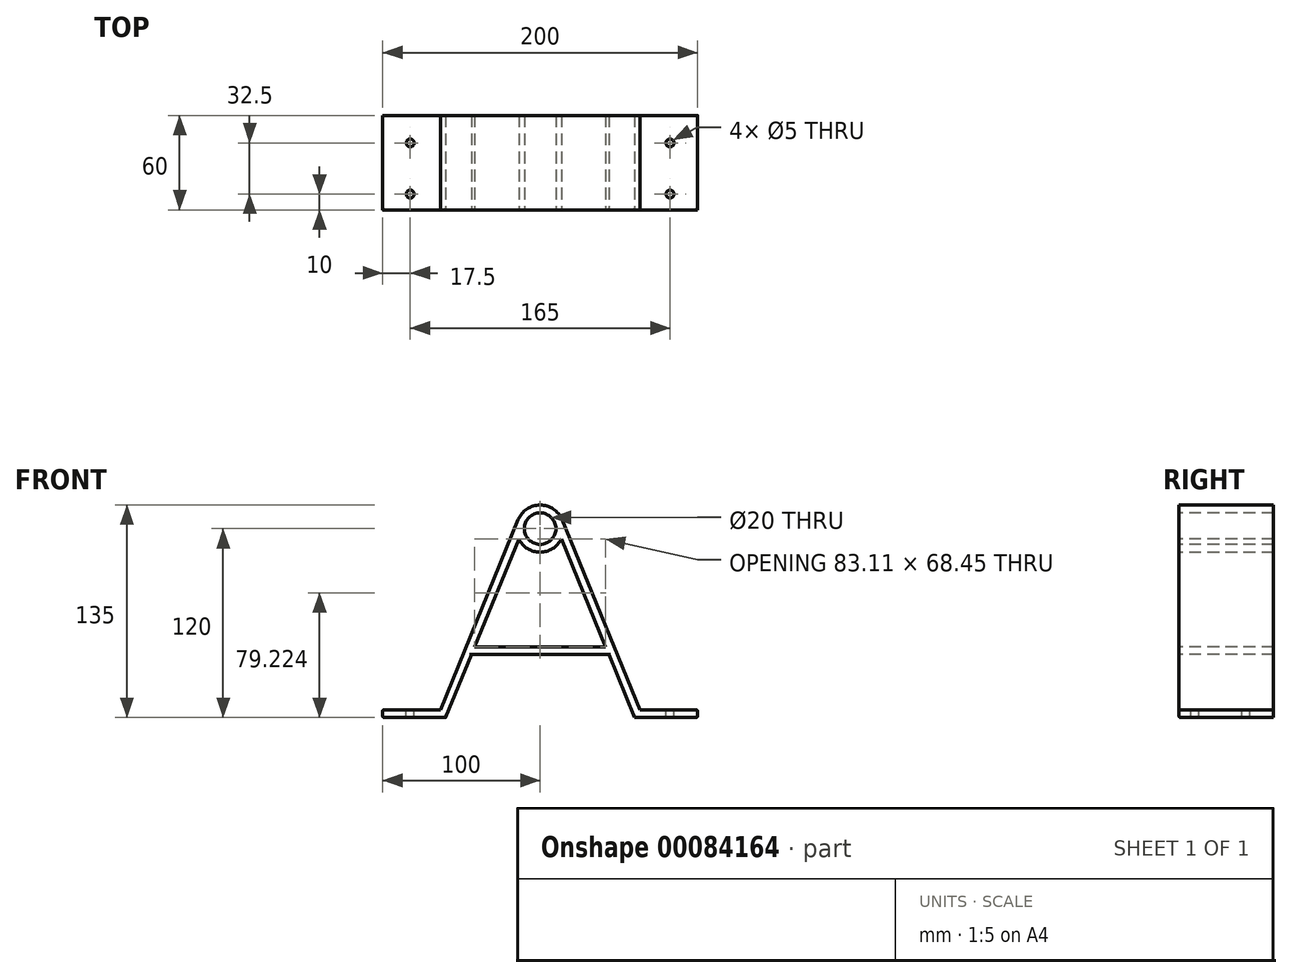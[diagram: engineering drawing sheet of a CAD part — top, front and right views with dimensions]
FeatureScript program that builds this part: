
annotation { "Feature Type Name" : "Feature", "Feature Type Description" : "" }
export const myFeature = defineFeature(function(context is Context, id is Id, definition is map)
    precondition{}
    {
        {
            var Q0;
            Q0=qCreatedBy(makeId("Front.planeOp"),FACE);
            var sketch = newSketch(context, id + "F0", { "sketchPlane" : qUnion([Q0])});
            skArc(sketch, "E0", {"start": v(86.5, 108.45) * mm, "mid": v(100, 100) * mm, "end": v(113.5, 108.45) * mm});
            skLineSegment(sketch, "E1", {"start": v(0, 0) * mm, "end": v(36.65, 0) * mm});
            skLineSegment(sketch, "E2", {"start": v(36.65, 0) * mm, "end": v(86.12, 120.69) * mm});
            skLineSegment(sketch, "E3", {"start": v(0, 0) * mm, "end": v(0, -5) * mm});
            skLineSegment(sketch, "E4", {"start": v(0, -5) * mm, "end": v(40, -5) * mm});
            skLineSegment(sketch, "E5", {"start": v(40, -5) * mm, "end": v(56.4, 35) * mm});
            skLineSegment(sketch, "E6", {"start": v(100, 115) * mm, "end": v(100, -58.47) * mm, "construction": true});
            skLineSegment(sketch, "E7.MirrorCS", {"start": v(160, -5) * mm, "end": v(143.6, 35) * mm});
            skLineSegment(sketch, "E8.MirrorCS", {"start": v(163.35, 0) * mm, "end": v(113.88, 120.69) * mm});
            skLineSegment(sketch, "E9.MirrorCS", {"start": v(200, 0) * mm, "end": v(163.35, 0) * mm});
            skLineSegment(sketch, "E10.MirrorCS", {"start": v(200, -5) * mm, "end": v(160, -5) * mm});
            skLineSegment(sketch, "E11.MirrorCS", {"start": v(200, 0) * mm, "end": v(200, -5) * mm});
            skCircle(sketch, "E12", {"center": v(100, 115) * mm, "radius": 10 * mm});
            skLineSegment(sketch, "E13", {"start": v(58.45, 40) * mm, "end": v(141.55, 40) * mm});
            skLineSegment(sketch, "E14", {"start": v(56.4, 35) * mm, "end": v(143.6, 35) * mm});
            skLineSegment(sketch, "E15.trimOffspring", {"start": v(58.45, 40) * mm, "end": v(86.5, 108.45) * mm});
            skLineSegment(sketch, "E16.trimOffspring", {"start": v(141.55, 40) * mm, "end": v(113.5, 108.45) * mm});
            skArc(sketch, "E17.trimOffspring", {"start": v(113.88, 120.69) * mm, "mid": v(100, 130) * mm, "end": v(86.12, 120.69) * mm});
            skLineSegment(sketch, "E18", {"start": v(160, -5) * mm, "end": v(200, -5) * mm});
            skLineSegment(sketch, "E19", {"start": v(199.82, 0.68) * mm, "end": v(163.35, 0) * mm});
            skArc(sketch, "E20", {"start": v(100, 130) * mm, "mid": v(91.64, 102.54) * mm, "end": v(113.88, 120.69) * mm});
            skLineSegment(sketch, "E21", {"start": v(86.12, 120.69) * mm, "end": v(36.65, 0) * mm});
            skSolve(sketch);
        }
        {
            var Q0;
            Q0=qSketchRegion(id+"F0",true);
            extrude(context, id + "F1", {"entities" : qUnion([Q0]), "oppositeDirection" : true, "depth" : 60 * mm});
        }
        {
            var Q0;
            Q0=makeQuery(id+"F1.opExtrude","SWEPT_FACE",FACE,{"disambiguationData":[OSD([sQuery(id+"F0.wireOp",EDGE,"E9.MirrorCS")])]});
            var sketch = newSketch(context, id + "F2", { "sketchPlane" : qUnion([Q0])});
            skCircle(sketch, "E22", {"center": v(182.5, 10) * mm, "radius": 2.5 * mm});
            skCircle(sketch, "E23", {"center": v(182.5, 42.5) * mm, "radius": 2.5 * mm});
            skLineSegment(sketch, "E24", {"start": v(100, 0) * mm, "end": v(100, 124.34) * mm, "construction": true});
            skCircle(sketch, "E25.MirrorC", {"center": v(17.5, 10) * mm, "radius": 2.5 * mm});
            skCircle(sketch, "E26.MirrorC", {"center": v(17.5, 42.5) * mm, "radius": 2.5 * mm});
            skSolve(sketch);
        }
        {
            var Q0;
            Q0=qSketchRegion(id+"F2",true);
            extrude(context, id + "F3", {"entities" : qUnion([Q0]), "operationType" : NewBodyOperationType.REMOVE, "endBound" : BoundingType.THROUGH_ALL, "oppositeDirection" : true, "depth" : 25 * mm});
        }
        {
            var Q0;
            Q0=makeQuery(id+"F1.opExtrude","SWEPT_EDGE",EDGE,{"disambiguationData":[OSD([sQuery(id+"F0.wireOp",EDGE,"E9.MirrorCS"),sQuery(id+"F0.wireOp",EDGE,"E11.MirrorCS")])]});
            var Q1;
            Q1=makeQuery(id+"F1.opExtrude","SWEPT_EDGE",EDGE,{"disambiguationData":[OSD([sQuery(id+"F0.wireOp",EDGE,"E10.MirrorCS"),sQuery(id+"F0.wireOp",EDGE,"E11.MirrorCS")])]});
            var Q2;
            Q2=makeQuery(id+"F1.opExtrude","SWEPT_EDGE",EDGE,{"disambiguationData":[OSD([sQuery(id+"F0.wireOp",EDGE,"E1"),sQuery(id+"F0.wireOp",EDGE,"E3")])]});
            var Q3;
            Q3=makeQuery(id+"F1.opExtrude","SWEPT_EDGE",EDGE,{"disambiguationData":[OSD([sQuery(id+"F0.wireOp",EDGE,"E3"),sQuery(id+"F0.wireOp",EDGE,"E4")])]});
            var Q4;
            Q4=makeQuery(id+"F1.opExtrude","CAP_EDGE",EDGE,{"disambiguationData":[OSD([sQuery(id+"F0.wireOp",EDGE,"E7.MirrorCS")])],"isStart":true});
            var Q5;
            Q5=makeQuery(id+"F1.opExtrude","CAP_EDGE",EDGE,{"disambiguationData":[OSD([sQuery(id+"F0.wireOp",EDGE,"E10.MirrorCS")])],"isStart":true});
            var Q6;
            Q6=makeQuery(id+"F1.opExtrude","CAP_EDGE",EDGE,{"disambiguationData":[OSD([sQuery(id+"F0.wireOp",EDGE,"E4")])],"isStart":true});
            var Q7;
            Q7=makeQuery(id+"F1.opExtrude","CAP_EDGE",EDGE,{"disambiguationData":[OSD([sQuery(id+"F0.wireOp",EDGE,"E5")])],"isStart":true});
            fillet(context, id + "F4", {"entities" : qUnion([Q0, Q1, Q2, Q3, Q4, Q5, Q6, Q7]), "radius" : 1 * mm, "tangentPropagation" : true, "allowEdgeOverflow" : false});
        }
    });
